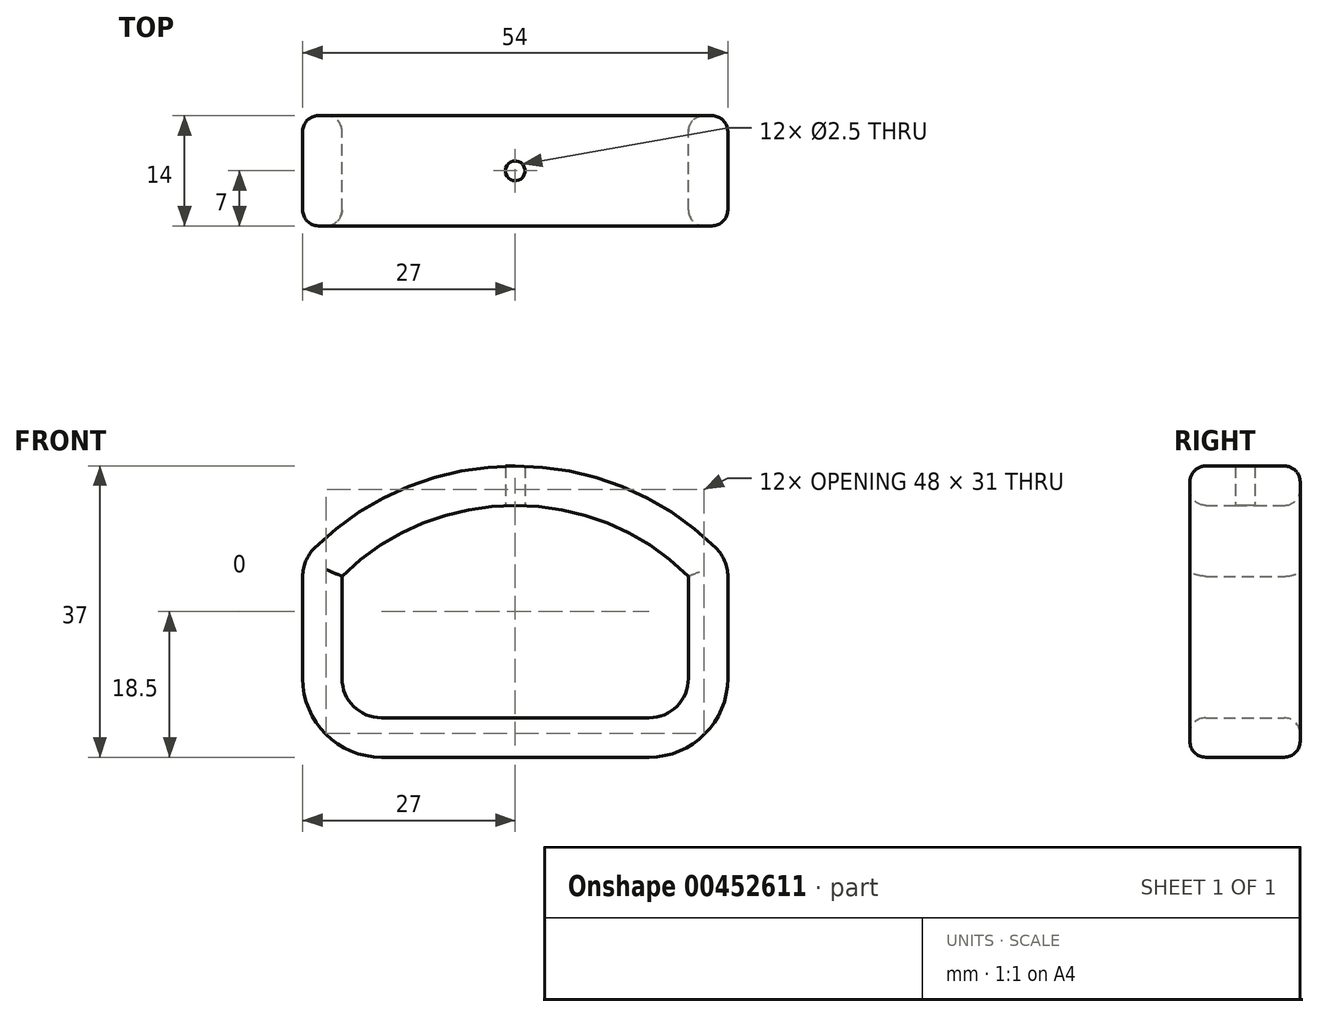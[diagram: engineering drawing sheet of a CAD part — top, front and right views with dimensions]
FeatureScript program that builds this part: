
annotation { "Feature Type Name" : "Feature", "Feature Type Description" : "" }
export const myFeature = defineFeature(function(context is Context, id is Id, definition is map)
    precondition{}
    {
        {
            var Q0;
            Q0=qCreatedBy(makeId("Front.planeOp"),FACE);
            var sketch = newSketch(context, id + "F0", { "sketchPlane" : qUnion([Q0])});
            skLineSegment(sketch, "E0.top", {"start": v(27, 6) * mm, "end": v(-27, 6) * mm});
            skLineSegment(sketch, "E0.left", {"start": v(27, -6) * mm, "end": v(27, 6) * mm});
            skLineSegment(sketch, "E0.right", {"start": v(-27, -6) * mm, "end": v(-27, 6) * mm});
            skPoint(sketch, "E0.middle", {"position": v(0, 0) * mm});
            skArc(sketch, "E1", {"start": v(25.5, -4.44) * mm, "mid": v(0, 6) * mm, "end": v(-25.5, -4.44) * mm});
            skLineSegment(sketch, "E2.right", {"start": v(27, -6) * mm, "end": v(27, -6) * mm});
            skLineSegment(sketch, "E3.top", {"start": v(17, -31) * mm, "end": v(-17, -31) * mm});
            skLineSegment(sketch, "E3.left", {"start": v(27, -8) * mm, "end": v(27, -21) * mm});
            skLineSegment(sketch, "E3.right", {"start": v(-27, -8) * mm, "end": v(-27, -21) * mm});
            skPoint(sketch, "E4.visualSharp", {"position": v(-27, -31) * mm});
            skArc(sketch, "E4.filletArc", {"start": v(-27, -21) * mm, "mid": v(-24.07, -28.07) * mm, "end": v(-17, -31) * mm});
            skPoint(sketch, "E5.visualSharp", {"position": v(27, -31) * mm});
            skArc(sketch, "E5.filletArc", {"start": v(17, -31) * mm, "mid": v(24.07, -28.07) * mm, "end": v(27, -21) * mm});
            skPoint(sketch, "E6.middle", {"position": v(0, -16.05) * mm});
            skPoint(sketch, "E7.visualSharp", {"position": v(-22, -26) * mm});
            skPoint(sketch, "E8.visualSharp", {"position": v(22, -26) * mm});
            skPoint(sketch, "E9.visualSharp", {"position": v(-27, -6) * mm});
            skArc(sketch, "E9.filletArc", {"start": v(-25.5, -4.44) * mm, "mid": v(-26.61, -6.07) * mm, "end": v(-27, -8) * mm});
            skPoint(sketch, "E10.visualSharp", {"position": v(27, -6) * mm});
            skArc(sketch, "E10.filletArc", {"start": v(27, -8) * mm, "mid": v(26.61, -6.07) * mm, "end": v(25.5, -4.44) * mm});
            skLineSegment(sketch, "E11.0", {"start": v(22, -8) * mm, "end": v(22, -21) * mm});
            skLineSegment(sketch, "E11.1", {"start": v(-22, -8) * mm, "end": v(-22, -21) * mm});
            skArc(sketch, "E11.2", {"start": v(-22, -21) * mm, "mid": v(-20.54, -24.54) * mm, "end": v(-17, -26) * mm});
            skArc(sketch, "E11.3", {"start": v(22, -8) * mm, "mid": v(0, 1) * mm, "end": v(-22, -8) * mm});
            skLineSegment(sketch, "E11.4", {"start": v(17, -26) * mm, "end": v(-17, -26) * mm});
            skArc(sketch, "E11.5", {"start": v(17, -26) * mm, "mid": v(20.54, -24.54) * mm, "end": v(22, -21) * mm});
            skSolve(sketch);
        }
        {
            var Q0;
            Q0=makeQuery(id+"F0.imprint","IMPRINT",FACE,{"disambiguationData":[TD([[makeQuery(id+"F0.imprint","IMPRINT",EDGE,{"derivedFrom":sQuery(id+"F0.wireOp",EDGE,"E3.top")}),-1.0]])]});
            extrude(context, id + "F1", {"entities" : qUnion([Q0]), "depth" : 14 * mm});
        }
        {
            var Q0;
            Q0=qCreatedBy(makeId("Top.planeOp"),FACE);
            var sketch = newSketch(context, id + "F2", { "sketchPlane" : qUnion([Q0])});
            skCircle(sketch, "E12", {"center": v(0, -7) * mm, "radius": 1.25 * mm});
            skLineSegment(sketch, "E13.0.0", {"start": v(-17, 0) * mm, "end": v(17, 0) * mm});
            skLineSegment(sketch, "E13.0.1", {"start": v(17, 0) * mm, "end": v(17, -14) * mm});
            skLineSegment(sketch, "E13.0.2", {"start": v(17, -14) * mm, "end": v(-17, -14) * mm});
            skLineSegment(sketch, "E13.0.3", {"start": v(-17, -14) * mm, "end": v(-17, 0) * mm});
            skLineSegment(sketch, "E14", {"start": v(0, -14) * mm, "end": v(0, 0) * mm});
            skSolve(sketch);
        }
        {
            var Q0;
            {var subQ0=sQuery(id+"F2.wireOp",EDGE,"E14");var subQ1=sQuery(id+"F2.wireOp",EDGE,"E12");var subQ2=makeQuery(id+"F2.imprint","INTERSECT",VERTEX,{"disambiguationData":[OD(0.0)],"derivedFrom":[subQ1,subQ0]});Q0=makeQuery(id+"F2.imprint","IMPRINT",FACE,{"disambiguationData":[TD([[makeQuery(id+"F2.imprint","IMPRINT",EDGE,{"disambiguationData":[TD([[subQ2,-1.0]])],"derivedFrom":subQ1}),1.0]])]});}
            var Q1;
            {var subQ0=sQuery(id+"F2.wireOp",EDGE,"E14");var subQ1=sQuery(id+"F2.wireOp",EDGE,"E12");var subQ2=makeQuery(id+"F2.imprint","INTERSECT",VERTEX,{"disambiguationData":[OD(0.0)],"derivedFrom":[subQ1,subQ0]});Q1=makeQuery(id+"F2.imprint","IMPRINT",FACE,{"disambiguationData":[TD([[makeQuery(id+"F2.imprint","IMPRINT",EDGE,{"disambiguationData":[TD([[subQ2,1.0]])],"derivedFrom":subQ1}),1.0]])]});}
            extrude(context, id + "F3", {"entities" : qUnion([Q0, Q1]), "operationType" : NewBodyOperationType.REMOVE, "depth" : 23.7 * mm});
        }
        {
            var Q0;
            Q0=makeQuery(id+"F1.opExtrude","CAP_EDGE",EDGE,{"disambiguationData":[OSD([sQuery(id+"F0.wireOp",EDGE,"E11.3")])],"isStart":false});
            var Q1;
            Q1=makeQuery(id+"F1.opExtrude","CAP_EDGE",EDGE,{"disambiguationData":[OSD([sQuery(id+"F0.wireOp",EDGE,"E11.0")])],"isStart":false});
            var Q2;
            Q2=makeQuery(id+"F1.opExtrude","CAP_EDGE",EDGE,{"disambiguationData":[OSD([sQuery(id+"F0.wireOp",EDGE,"E11.5")])],"isStart":false});
            var Q3;
            Q3=makeQuery(id+"F1.opExtrude","CAP_EDGE",EDGE,{"disambiguationData":[OSD([sQuery(id+"F0.wireOp",EDGE,"E11.4")])],"isStart":true});
            var Q4;
            Q4=makeQuery(id+"F1.opExtrude","CAP_EDGE",EDGE,{"disambiguationData":[OSD([sQuery(id+"F0.wireOp",EDGE,"E11.3")])],"isStart":true});
            var Q5;
            Q5=makeQuery(id+"F1.opExtrude","CAP_EDGE",EDGE,{"disambiguationData":[OSD([sQuery(id+"F0.wireOp",EDGE,"E3.top")])],"isStart":true});
            var Q6;
            Q6=makeQuery(id+"F1.opExtrude","CAP_EDGE",EDGE,{"disambiguationData":[OSD([sQuery(id+"F0.wireOp",EDGE,"E3.top")])],"isStart":false});
            fillet(context, id + "F4", {"entities" : qUnion([Q0, Q1, Q2, Q3, Q4, Q5, Q6]), "radius" : 2 * mm, "tangentPropagation" : true, "allowEdgeOverflow" : false});
        }
    });
